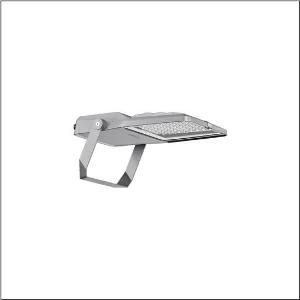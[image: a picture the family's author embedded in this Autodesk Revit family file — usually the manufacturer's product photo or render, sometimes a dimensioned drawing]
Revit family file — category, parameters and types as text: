
# Revit family: floodlight_fl_21_iq_mini___pl33t_5xa7771b4f1a_48a0
name_source: partatom
category: Lighting Fixtures
units: mm (PartAtom-declared; Revit-internal decimal feet)

## family parameters
Cut with Voids When Loaded = No
Host = Face
Light Source = No
Part Type = Normal
Room Calculation Point = No
Round Connector Dimension = Use Diameter
Shared = No

## types (1)
- --- (1 x LED, 6420 lm, 45.5 W, 4000K)
    Apparent Load = 46 VA
    CIE Flux Codes = 26 75 99 100 100
    Color Rendering = 70
    Color Temperature = 4000K
    Default Elevation = 1800 mm
    Description = Floodlight FL 21 iQ mini, floodlight, primary light control with lens, of PMMA, primary optical cover: protective disc, of toughened safety glass, transparent, light distribution: PL33T, light emission: direct distribution, installation type: surface-mounted, LED, High Power LED, rated luminous flux: 6.420lm, luminous efficacy: 141lm/W, light colour: 740, colour temperature: 4000K, control: Auto-Match, Temp-Guard, Lumen-Switch, Night-Set, Smart-Wire, Light-Fading, Desk-Remote (wireless, voltage-free reading and setting of iQ features in the workshop via application-optimized NFC function/RFID function), optimised constant luminous flux control (CLO 2.0), with terminal, 6-pole, mains connection: 220..240V, AC, 50/60Hz, start of lifetime: 46W, end of service life: 48W, reduction: 22W, luminaire housing, of diecast aluminium, powder-coated, Siteco® metallic grey (DB 702S), corrosivity category C5 mid according to DIN EN ISO 12944, sealing non-destructively replaceable, mounting bracket, of steel, galvanised, powder-coated, Siteco® metallic grey (DB 702S), protection rating (complete): IP66, insulation class (complete): insulation class II (safety insulation), certification: CE, ENEC, VDE, protection symbol: D, impact resistance: IK08, permissible operating ambient temperature: -40..+40°C, permissible operating ambient temperature for outdoor applications: -40..+50°C, standard: DIN EN 12944, LABS conformity tested according to VDMA 24364:2018-05, packaging unit: 1 piece

Light Distribution: PL33T
    Height = 70 mm
    Lamp = 1 x LED
    Lamp Light Flux = 6420 lm
    Lamp Power = 45.5 W
    Lamp count = 1
    Length = 485 mm
    Luminous efficacy = 141 lm/W
    Manufacturer = Siteco
    ModVariant = No
    Model = 5XA7771B4F1A
    Mounting Place = Wall
    Mounting Type = Surface mounted
    Number of Poles = 1
    OnlyDefault = Yes
    Power Factor = 1
    Product Name = Floodlight FL 21 iQ mini | PL33T
    Product group = floodlight | wall mounted
    ProductGroupID = 2001
    Protection Class = Protection class II
    Protection Degree = IP 66
    RLX_Detail_Level = 1
    RLX_Emergency_Light_Flux = 0 lm
    RLX_Emergency_Type = 0
    RLX_Emergency_Type_DB = No
    RlxData = <blob elided: 96065 chars, md5=9037ef79>
    Socket = socket
    Standby Power = 0 W
    System Light Flux = 6420 lm
    System Power = 46 W
    Type Comments = factory setting: luminous flux: 100 % | dim-lin: 254 | 463 mA
    Type Image = l_1006845.jpg
    URL = http://relux.com
    VarID = @adj_082731
    Voltage = 0 V
    Weight = 0.00 kg
    Width = 337 mm

## geometry (parser evidence)
native form markers: Blend x4, Sweep x11
no freeform markers — native parametric forms only
